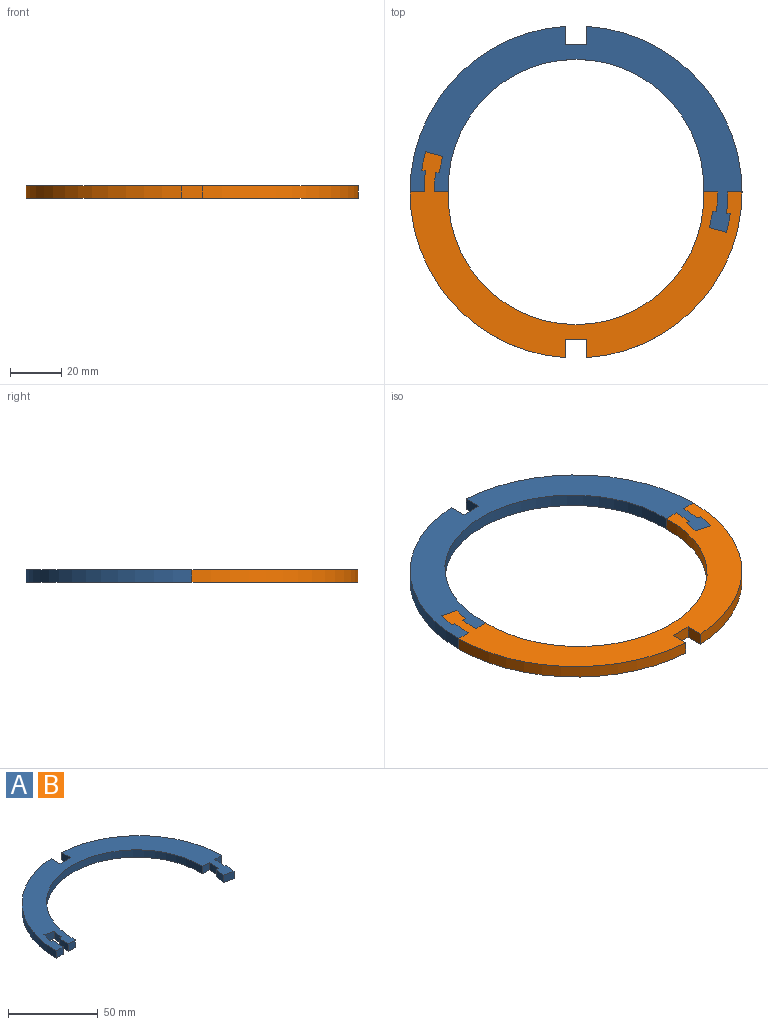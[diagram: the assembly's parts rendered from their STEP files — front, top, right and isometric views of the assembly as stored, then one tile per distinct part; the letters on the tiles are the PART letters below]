
ASSEMBLY  parts=2 mates=1
PART A: 26 faces, bbox 130x80.7x5 mm
  f0: plane 5x1.49mm, normal (0.14,0.99,0), area 7.5mm2, adj f1,f23,f24,f25
  f1: cylinder r=54mm len=6.46mm, axis (0,0,-1), area 33mm2, adj f0,f2,f24,f25
  f2: plane 6.76x5mm, normal (-0.26,-0.97,0), area 35mm2, adj f1,f3,f24,f25
  f3: cylinder r=61mm len=7.3mm, axis (0,0,-1), area 37.3mm2, adj f2,f4,f24,f25
  f4: plane 5x1.49mm, normal (0.14,0.99,0), area 7.5mm2, adj f3,f5,f24,f25
  f5: cylinder r=59.5mm len=8.28mm, axis (0,0,-1), area 41.5mm2, adj f4,f6,f24,f25
  f6: plane 5.5x5mm, normal (0,-1,0), area 27.5mm2, adj f5,f7,f24,f25
  f7: cylinder r=65mm len=64.87mm, axis (0,0,-1), area 489.9mm2, adj f6,f8,f24,f25
  f8: plane 6.95x5mm, normal (-1,0,0), area 34.8mm2, adj f7,f9,f24,f25
  f9: plane 8.25x5mm, normal (0,1,0), area 41.3mm2, adj f8,f10,f24,f25
  f10: plane 6.95x5mm, normal (1,0,0), area 34.8mm2, adj f9,f11,f24,f25
  f11: cylinder r=65mm len=64.87mm, axis (0,0,-1), area 489.9mm2, adj f10,f12,f24,f25
  f12: plane 5.5x5mm, normal (0,-1,0), area 27.5mm2, adj f11,f13,f24,f25
  f13: cylinder r=59.5mm len=8.28mm, axis (0,0,-1), area 41.5mm2, adj f12,f14,f24,f25
  f14: plane 5x1.49mm, normal (0.14,0.99,0), area 7.5mm2, adj f13,f15,f24,f25
  f15: cylinder r=61mm len=7.3mm, axis (0,0,-1), area 37.3mm2, adj f14,f16,f24,f25
  f16: plane 6.76x5mm, normal (-0.26,-0.97,0), area 35mm2, adj f15,f17,f24,f25
  f17: cylinder r=54mm len=6.46mm, axis (0,0,-1), area 33mm2, adj f16,f18,f24,f25
  f18: plane 5x1.49mm, normal (0.14,0.99,0), area 7.5mm2, adj f17,f19,f24,f25
  f19: cylinder r=55.5mm len=7.72mm, axis (0,0,-1), area 38.7mm2, adj f18,f20,f24,f25
  f20: plane 5.54x5mm, normal (0,-1,0), area 27.7mm2, adj f19,f21,f24,f25
  f21: cylinder r=50mm len=100mm, axis (0,0,-1), area 804.6mm2, adj f20,f22,f24,f25
  f22: plane 5.54x5mm, normal (0,-1,0), area 27.7mm2, adj f21,f23,f24,f25
  f23: cylinder r=55.5mm len=7.72mm, axis (0,0,-1), area 38.7mm2, adj f0,f22,f24,f25
  f24: plane 130x80.66mm, normal (0,0,1), area 2460mm2, adj f0,f1,f2,f3,f4,f5,f6,f7
  f25: plane 130x80.66mm, normal (0,0,-1), area 2460mm2, adj f0,f1,f2,f3,f4,f5,f6,f7
PART B: same geometry as A
PLACE A t=(12.78,48.36,-4.89)mm
PLACE B rot(axis=(0,0,-1),180deg) t=(12.78,48.36,-4.89)mm
MATE fastened B.f2 <-> A.f16  axis (0.26,0.97,0) through (-42.76,63.24,-2.39)mm
